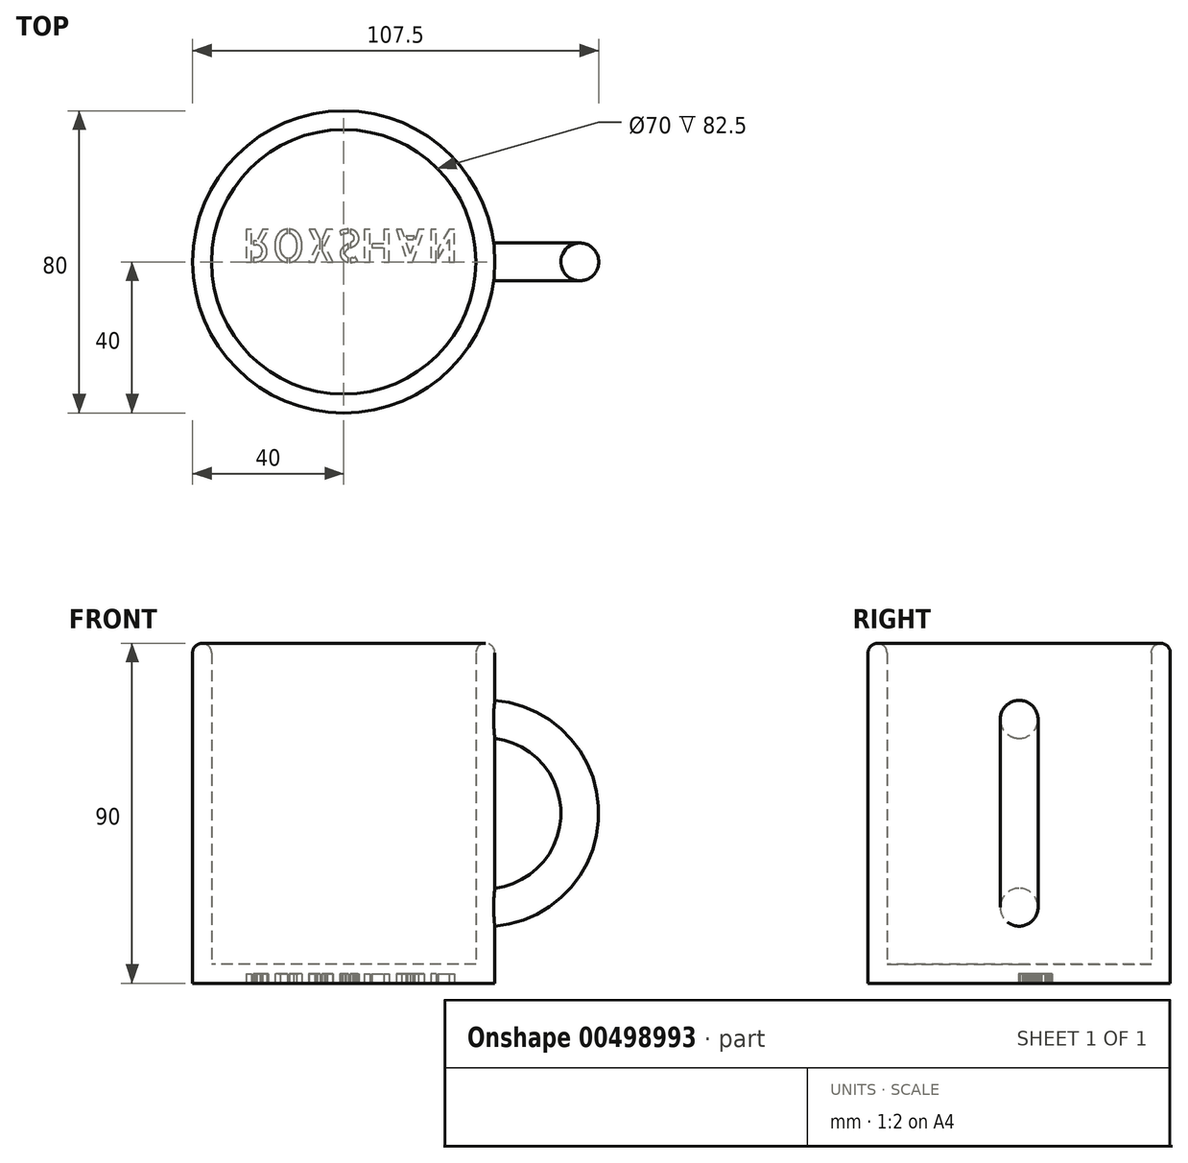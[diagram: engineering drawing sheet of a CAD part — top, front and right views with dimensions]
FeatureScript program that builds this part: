
annotation { "Feature Type Name" : "Feature", "Feature Type Description" : "" }
export const myFeature = defineFeature(function(context is Context, id is Id, definition is map)
    precondition{}
    {
        {
            var Q0;
            Q0=qCreatedBy(makeId("Top.planeOp"),FACE);
            var sketch = newSketch(context, id + "F0", { "sketchPlane" : qUnion([Q0])});
            skCircle(sketch, "E0", {"center": v(0, 0) * mm, "radius": 40 * mm});
            skSolve(sketch);
        }
        {
            var Q0;
            Q0=qSketchRegion(id+"F0",true);
            extrude(context, id + "F1", {"entities" : qUnion([Q0]), "depth" : 90 * mm});
        }
        {
            var Q0;
            Q0=makeQuery(id+"F1.opExtrude","CAP_FACE",FACE,{"disambiguationData":[OSD([sQuery(id+"F0.wireOp",EDGE,"E0")])],"isStart":false});
            shell(context, id + "F2", {"entities" : qUnion([Q0]), "thickness" : 5 * mm});
        }
        {
            var Q0;
            Q0=qCreatedBy(makeId("Right.planeOp"),FACE);
            cPlane(context, id + "F3", {"entities" : qUnion([Q0]), "cplaneType" : CPlaneType.OFFSET, "offset" : 37.5 * mm, "width" : 150 * mm, "height" : 150 * mm});
        }
        {
            var Q0;
            Q0=qCreatedBy(id+"F3.planeOp",FACE);
            var sketch = newSketch(context, id + "F4", { "sketchPlane" : qUnion([Q0])});
            skCircle(sketch, "E1", {"center": v(0, 70) * mm, "radius": 5 * mm});
            skLineSegment(sketch, "E2", {"start": v(0, 45) * mm, "end": v(36, 45) * mm});
            skSolve(sketch);
        }
        {
            var Q0;
            Q0=qSketchRegion(id+"F4",true);
            var Q1;
            Q1=sQuery(id+"F4.wireOp",EDGE,"E2");
            revolve(context, id + "F5", {"operationType" : NewBodyOperationType.ADD, "entities" : qUnion([Q0]), "axis" : qUnion([Q1]), "revolveType" : RevolveType.ONE_DIRECTION, "angle" : 180 * degree});
        }
        {
            var Q0;
            {var subQ0=sQuery(id+"F0.wireOp",EDGE,"E0");Q0=makeQuery(id+"F2.opShell","OFFSET_EDGE",EDGE,{"disambiguationData":[OSD([subQ0]),TDD([makeQuery(id+"F1.opExtrude","CAP_EDGE",EDGE,{"disambiguationData":[OSD([subQ0])],"isStart":false})])]});}
            var Q1;
            Q1=makeQuery(id+"F1.opExtrude","CAP_EDGE",EDGE,{"disambiguationData":[OSD([sQuery(id+"F0.wireOp",EDGE,"E0")])],"isStart":false});
            fillet(context, id + "F6", {"entities" : qUnion([Q0, Q1]), "radius" : 2.5 * mm, "tangentPropagation" : true, "allowEdgeOverflow" : false});
        }
        {
            var Q0;
            Q0=makeQuery(id+"F1.opExtrude","CAP_FACE",FACE,{"disambiguationData":[OSD([sQuery(id+"F0.wireOp",EDGE,"E0")])],"isStart":true});
            var sketch = newSketch(context, id + "F7", { "sketchPlane" : qUnion([Q0])});
            skText(sketch, "E3", { "text": "ROXSHAN", "fontName": "OpenSans-BoldItalic.ttf"});
            const initialGuessF7  = {"E3": [-0.02451, -0.00713, 1, 0, 0.00713]};
            skSetInitialGuess(sketch, initialGuessF7);
            skSolve(sketch);
        }
        {
            var Q0;
            Q0=qSketchRegion(id+"F7",true);
            extrude(context, id + "F8", {"entities" : qUnion([Q0]), "operationType" : NewBodyOperationType.ADD, "oppositeDirection" : true, "depth" : 2.5 * mm});
        }
        {
            var Q0;
            Q0=makeQuery(id+"F1.opExtrude","CAP_FACE",FACE,{"disambiguationData":[OSD([sQuery(id+"F0.wireOp",EDGE,"E0")])],"isStart":true});
            var sketch = newSketch(context, id + "F9", { "sketchPlane" : qUnion([Q0])});
            skText(sketch, "E4", { "text": "ROXSHAN", "fontName": "AllertaStencil-Regular.ttf"});
            const initialGuessF9  = {"E4": [-0.02685, -0.00862, 1, 0, 0.00862]};
            skSetInitialGuess(sketch, initialGuessF9);
            skSolve(sketch);
        }
        {
            var Q0;
            Q0=qSketchRegion(id+"F9",true);
            extrude(context, id + "F10", {"entities" : qUnion([Q0]), "operationType" : NewBodyOperationType.REMOVE, "oppositeDirection" : true, "depth" : 2.5 * mm});
        }
    });
